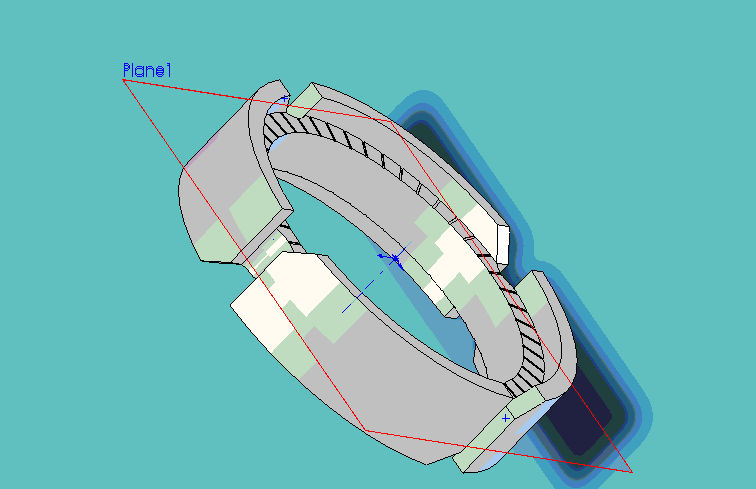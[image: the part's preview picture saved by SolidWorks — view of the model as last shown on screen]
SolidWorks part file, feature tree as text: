
SOLIDWORKS PART (.sldprt)
format: sldprt  version: not decoded by parser v0  size: 1,081,856 bytes
history: native  units: mm
features: sketch x6, plane x4, cut_extrude x4, extrude x2, pattern_circular x2, material x1, mirror x1 (+10 scaffold rows collapsed)
feature tree (30):
  scaffold x10  (default folders/planes/origin — collapsed)
  material  "Material <not specified>"
  plane  "Frontal"
  plane  "Horizontal"
  plane  "Profile"
  sketch  "Sketch1"  dims[D1=~17.094595mm]
  extrude  "Extrude1"  Depth=4mm
  sketch  "Sketch2"  dims[D1=0.2mm]
  cut_extrude  "Cut-Extrude1"  Depth=0.05mm
  pattern_circular  "CirPattern1"  Count=48 Angle=7.5deg
  plane  "Plane1"  Offset=2mm
  mirror  "Mirror1"
  sketch  "Sketch4"  dims[D1=32.0mm]
  extrude  "Extrude2"  Depth=8mm
  sketch  "Sketch5"  dims[D2=2.0mm D1=2.5mm]
  cut_extrude  "Cut-Extrude6"  [1 undecoded]
  sketch  "Sketch6"  dims[c1.D1=2.0mm c1.D2=2.0mm c2.D2=45.0deg]
  cut_extrude  "Cut-Extrude7"  [1 undecoded]
  sketch  "Sketch7"  dims[c1.D1=2.0mm c1.D2=2.0mm c2.D2=45.0deg]
  cut_extrude  "Cut-Extrude9"  [1 undecoded]
  pattern_circular  "CirPattern2"  Count=4 Angle=360deg
decode coverage: 11 of 15 modeling features carry decoded parameters
note: ~ marks probable driven/reference dimensions
note: 3 parameter values undecoded
summary: no parameter record found for 3 features
note: suppression state not decoded; provenance and decode notes live in map.json
